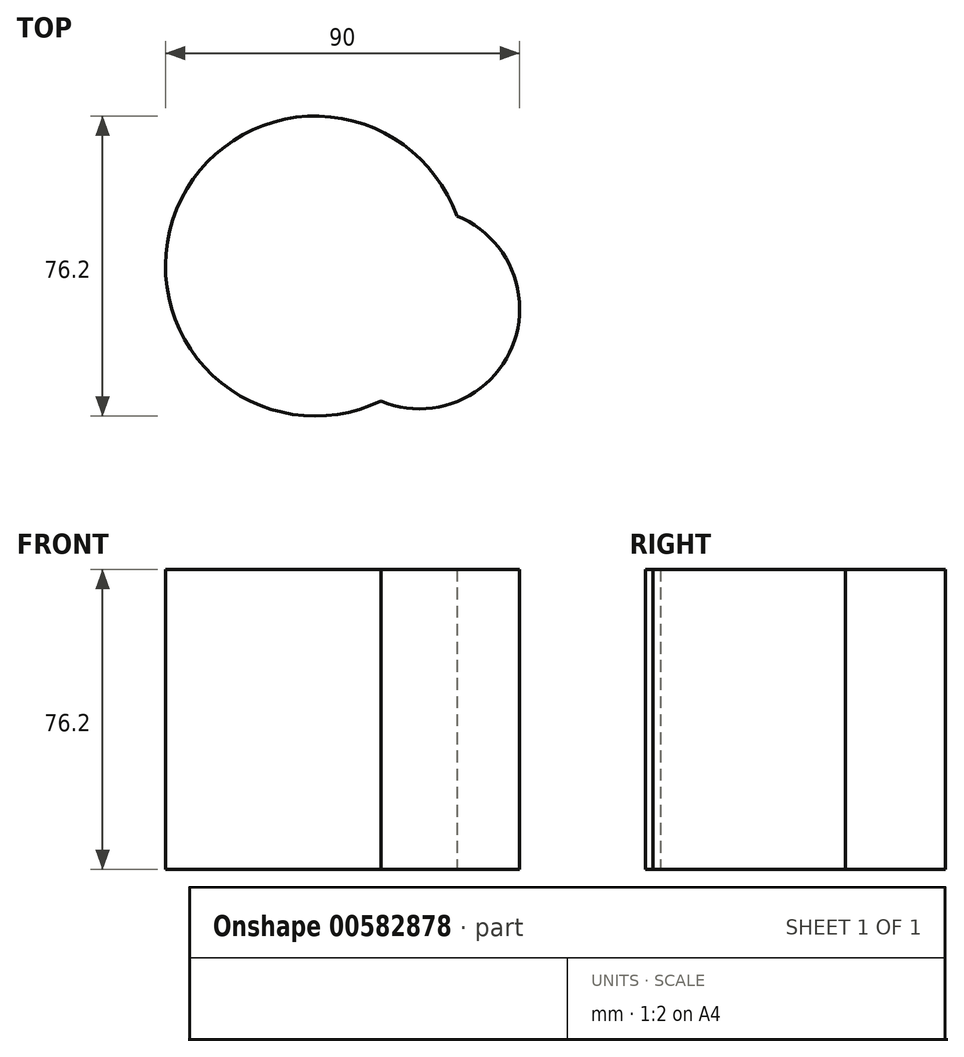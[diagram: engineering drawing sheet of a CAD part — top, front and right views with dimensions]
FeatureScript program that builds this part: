
annotation { "Feature Type Name" : "Feature", "Feature Type Description" : "" }
export const myFeature = defineFeature(function(context is Context, id is Id, definition is map)
    precondition{}
    {
        {
            var Q0;
            Q0=qCreatedBy(makeId("Top.planeOp"),FACE);
            var sketch = newSketch(context, id + "F0", { "sketchPlane" : qUnion([Q0])});
            skCircle(sketch, "E0", {"center": v(-76.7, 35.42) * mm, "radius": 50.8 * mm});
            skCircle(sketch, "E1", {"center": v(-26.5, 10.88) * mm, "radius": 38.1 * mm});
            skCircle(sketch, "E2", {"center": v(0, 0) * mm, "radius": 25.4 * mm});
            skSolve(sketch);
        }
        {
            var Q0;
            {var subQ0=sQuery(id+"F0.wireOp",EDGE,"E2");var subQ1=sQuery(id+"F0.wireOp",EDGE,"E1");var subQ2=makeQuery(id+"F0.imprint","INTERSECT",VERTEX,{"disambiguationData":[OD(0.0)],"derivedFrom":[subQ1,subQ0]});Q0=makeQuery(id+"F0.imprint","IMPRINT",FACE,{"disambiguationData":[TD([[makeQuery(id+"F0.imprint","IMPRINT",EDGE,{"disambiguationData":[TD([[subQ2,1.0]])],"derivedFrom":subQ1}),-1.0]])]});}
            var Q1;
            {var subQ0=sQuery(id+"F0.wireOp",EDGE,"E1");var subQ1=sQuery(id+"F0.wireOp",EDGE,"E0");var subQ2=makeQuery(id+"F0.imprint","INTERSECT",VERTEX,{"disambiguationData":[OD(0.0)],"derivedFrom":[subQ1,subQ0]});Q1=makeQuery(id+"F0.imprint","IMPRINT",FACE,{"disambiguationData":[TD([[makeQuery(id+"F0.imprint","IMPRINT",EDGE,{"disambiguationData":[TD([[subQ2,1.0]])],"derivedFrom":subQ1}),-1.0]])]});}
            var Q2;
            {var subQ0=sQuery(id+"F0.wireOp",EDGE,"E1");var subQ1=sQuery(id+"F0.wireOp",EDGE,"E0");var subQ2=makeQuery(id+"F0.imprint","INTERSECT",VERTEX,{"disambiguationData":[OD(0.0)],"derivedFrom":[subQ1,subQ0]});Q2=makeQuery(id+"F0.imprint","IMPRINT",FACE,{"disambiguationData":[TD([[makeQuery(id+"F0.imprint","IMPRINT",EDGE,{"disambiguationData":[TD([[subQ2,1.0]])],"derivedFrom":subQ1}),1.0]])]});}
            var Q3;
            {var subQ0=sQuery(id+"F0.wireOp",EDGE,"E2");var subQ1=sQuery(id+"F0.wireOp",EDGE,"E1");var subQ2=makeQuery(id+"F0.imprint","INTERSECT",VERTEX,{"disambiguationData":[OD(0.0)],"derivedFrom":[subQ1,subQ0]});Q3=makeQuery(id+"F0.imprint","IMPRINT",FACE,{"disambiguationData":[TD([[makeQuery(id+"F0.imprint","IMPRINT",EDGE,{"disambiguationData":[TD([[subQ2,1.0]])],"derivedFrom":subQ1}),1.0]])]});}
            extrude(context, id + "F1", {"entities" : qUnion([Q0, Q1, Q2, Q3]), "depth" : 76.2 * mm, "offsetDistance" : 25.4 * mm});
        }
        {
            var Q0;
            Q0=sQuery(id+"F0.wireOp",EDGE,"E1");
            extrude(context, id + "F2", {"bodyType" : ToolBodyType.SURFACE, "surfaceEntities" : qUnion([Q0]), "oppositeDirection" : true, "depth" : 50.8 * mm, "offsetDistance" : 25.4 * mm});
        }
    });
